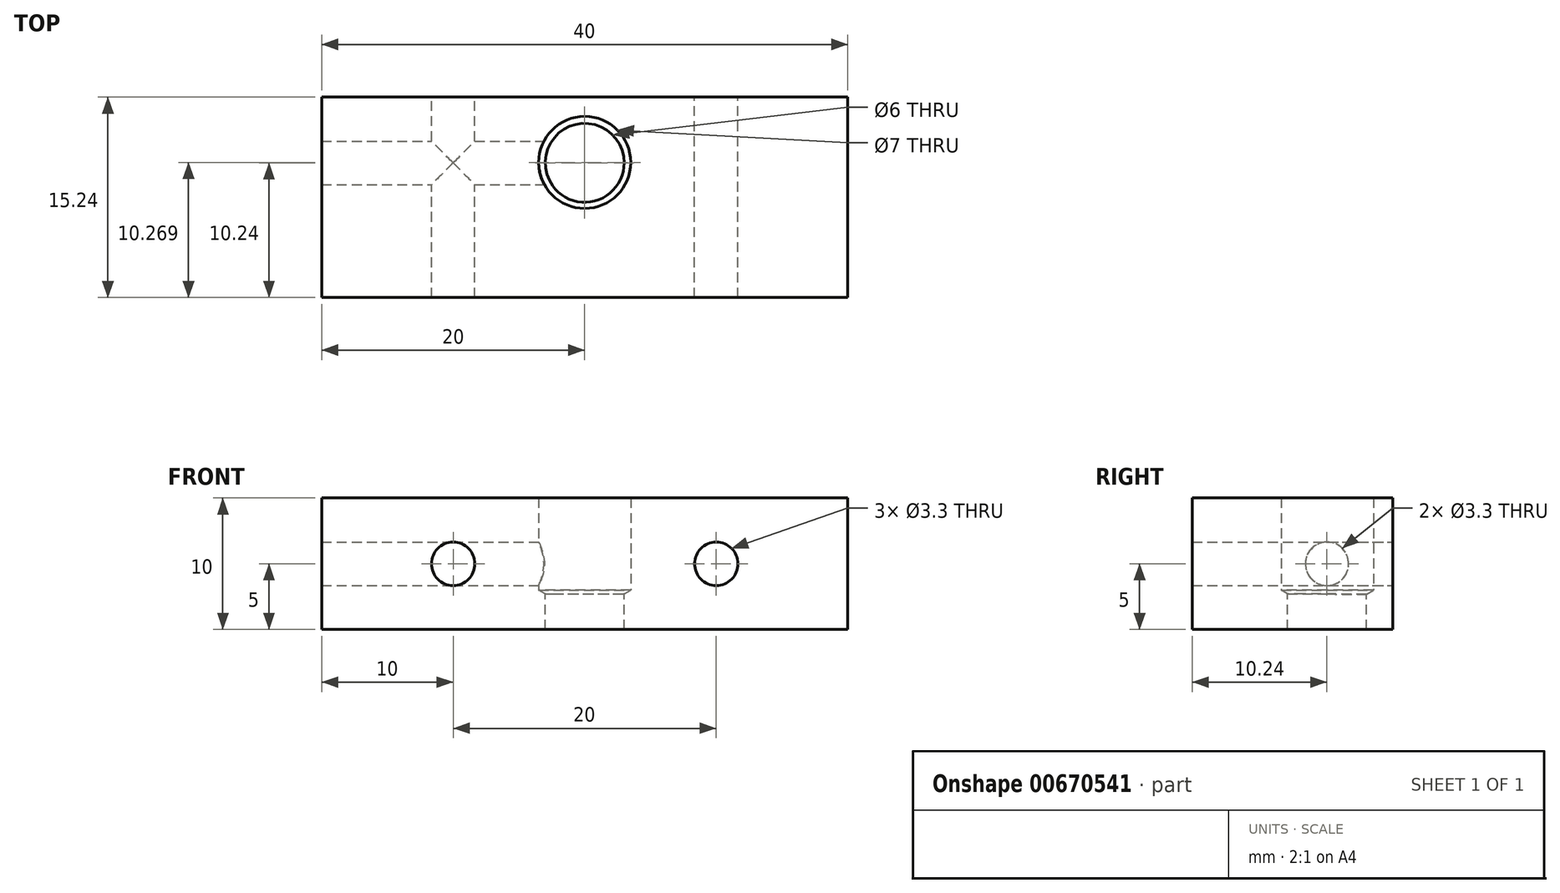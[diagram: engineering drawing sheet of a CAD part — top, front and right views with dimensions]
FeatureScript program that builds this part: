
annotation { "Feature Type Name" : "Feature", "Feature Type Description" : "" }
export const myFeature = defineFeature(function(context is Context, id is Id, definition is map)
    precondition{}
    {
        {
            var Q0;
            Q0=qCreatedBy(makeId("Top.planeOp"),FACE);
            var sketch = newSketch(context, id + "F0", { "sketchPlane" : qUnion([Q0])});
            skLineSegment(sketch, "E0.top", {"start": v(-20, -5) * mm, "end": v(20, -5) * mm});
            skLineSegment(sketch, "E0.left", {"start": v(-20, 10.24) * mm, "end": v(-20, -5) * mm});
            skLineSegment(sketch, "E0.right", {"start": v(20, 10.24) * mm, "end": v(20, -5) * mm});
            skLineSegment(sketch, "E1", {"start": v(-20, 10.24) * mm, "end": v(-9.42, 10.24) * mm});
            skLineSegment(sketch, "E2", {"start": v(20, 10.24) * mm, "end": v(10.65, 10.24) * mm});
            skLineSegment(sketch, "E3", {"start": v(-9.42, 10.24) * mm, "end": v(10.65, 10.24) * mm});
            skPoint(sketch, "E4", {"position": v(0, 5.24) * mm});
            skLineSegment(sketch, "E5.bottom", {"start": v(-20, 10.24) * mm, "end": v(-12, 10.24) * mm});
            skLineSegment(sketch, "E6.top", {"start": v(12, 10.24) * mm, "end": v(20, 10.24) * mm});
            skSolve(sketch);
        }
        {
            var Q0;
            Q0=makeQuery(id+"F0.imprint","IMPRINT",FACE,{"disambiguationData":[TD([[makeQuery(id+"F0.imprint","IMPRINT",EDGE,{"derivedFrom":sQuery(id+"F0.wireOp",EDGE,"E0.top")}),1.0]])]});
            extrude(context, id + "F1", {"entities" : qUnion([Q0]), "depth" : 10 * mm, "offsetDistance" : 25 * mm});
        }
        {
            var Q0;
            Q0=sQuery(id+"F0.wireOp",VERTEX,"E4");
            var Q1;
            Q1=makeQuery(id+"F1.opExtrude","SWEPT_BODY",BODY,{"disambiguationData":[OSD([sQuery(id+"F0.wireOp",EDGE,"E0.top"),sQuery(id+"F0.wireOp",EDGE,"E0.left"),sQuery(id+"F0.wireOp",EDGE,"E0.right"),sQuery(id+"F0.wireOp",EDGE,"E1"),sQuery(id+"F0.wireOp",EDGE,"E2"),sQuery(id+"F0.wireOp",EDGE,"E3")])]});
            hole(context, id + "F2", {"style" : HoleStyle.SIMPLE, "endStyle" : HoleEndStyle.THROUGH, "oppositeDirection" : true, "holeDiameter" : 6 * mm, "majorDiameter" : 5 * mm, "isTappedThrough" : true, "tappedDepth" : 10 * mm, "tapClearance" : 0, "locations" : qUnion([Q0]), "scope" : qUnion([Q1]), "startStyle" : HoleStartStyle.PART});
        }
        {
            var Q0;
            Q0=makeQuery(id+"F1.opExtrude","SWEPT_FACE",FACE,{"disambiguationData":[OSD([sQuery(id+"F0.wireOp",EDGE,"E0.top")])]});
            var sketch = newSketch(context, id + "F3", { "sketchPlane" : qUnion([Q0])});
            skPoint(sketch, "E7", {"position": v(-10, 5) * mm});
            skPoint(sketch, "E8", {"position": v(10, 5) * mm});
            skSolve(sketch);
        }
        {
            var Q0;
            Q0=sQuery(id+"F3.wireOp",VERTEX,"E7");
            var Q1;
            Q1=sQuery(id+"F3.wireOp",VERTEX,"E8");
            var Q2;
            Q2=makeQuery(id+"F1.opExtrude","SWEPT_BODY",BODY,{"disambiguationData":[OSD([sQuery(id+"F0.wireOp",EDGE,"E0.top"),sQuery(id+"F0.wireOp",EDGE,"E0.left"),sQuery(id+"F0.wireOp",EDGE,"E0.right"),sQuery(id+"F0.wireOp",EDGE,"E1"),sQuery(id+"F0.wireOp",EDGE,"E2"),sQuery(id+"F0.wireOp",EDGE,"E3"),sQuery(id+"F0.wireOp",EDGE,"E5.bottom"),sQuery(id+"F0.wireOp",EDGE,"E6.top")])]});
            hole(context, id + "F4", {"style" : HoleStyle.SIMPLE, "endStyle" : HoleEndStyle.BLIND, "standardTappedOrClearance" : lookupTablePath({ "standard" : "ISO", "engagement" : "75%", "pitch" : "0.7 mm", "size" : "M4", "type" : "Tapped" }), "standardBlindInLast" : lookupTablePath({ "standard" : "ISO", "engagement" : "75%", "pitch" : "0.7 mm", "size" : "M4", "type" : "Tapped" }), "holeDiameter" : 3.3 * mm, "majorDiameter" : 4 * mm, "showTappedDepth" : true, "holeDepth" : 15.5 * mm, "tappedDepth" : 15.5 * mm, "tapClearance" : 0, "locations" : qUnion([Q0, Q1]), "scope" : qUnion([Q2]), "startStyle" : HoleStartStyle.PART});
        }
        {
            var Q0;
            Q0=makeQuery(id+"F1.opExtrude","SWEPT_FACE",FACE,{"disambiguationData":[OSD([sQuery(id+"F0.wireOp",EDGE,"E0.left")])]});
            var sketch = newSketch(context, id + "F5", { "sketchPlane" : qUnion([Q0])});
            skPoint(sketch, "E9", {"position": v(-5.24, 5) * mm});
            skPoint(sketch, "E9.positionSnap0", {"position": v(-10.24, 5) * mm});
            skSolve(sketch);
        }
        {
            var Q0;
            Q0=sQuery(id+"F5.wireOp",VERTEX,"E9");
            var Q1;
            Q1=makeQuery(id+"F1.opExtrude","SWEPT_BODY",BODY,{"disambiguationData":[OSD([sQuery(id+"F0.wireOp",EDGE,"E0.top"),sQuery(id+"F0.wireOp",EDGE,"E0.left"),sQuery(id+"F0.wireOp",EDGE,"E0.right"),sQuery(id+"F0.wireOp",EDGE,"E1"),sQuery(id+"F0.wireOp",EDGE,"E2"),sQuery(id+"F0.wireOp",EDGE,"E3"),sQuery(id+"F0.wireOp",EDGE,"E5.bottom"),sQuery(id+"F0.wireOp",EDGE,"E6.top")])]});
            hole(context, id + "F6", {"style" : HoleStyle.SIMPLE, "endStyle" : HoleEndStyle.BLIND, "standardTappedOrClearance" : lookupTablePath({ "standard" : "ISO", "engagement" : "75%", "pitch" : "0.7 mm", "size" : "M4", "type" : "Tapped" }), "standardBlindInLast" : lookupTablePath({ "standard" : "ISO", "engagement" : "75%", "pitch" : "0.7 mm", "size" : "M4", "type" : "Tapped" }), "holeDiameter" : 3.3 * mm, "majorDiameter" : 4 * mm, "showTappedDepth" : true, "holeDepth" : 20 * mm, "tappedDepth" : 20 * mm, "tapClearance" : 0, "locations" : qUnion([Q0]), "scope" : qUnion([Q1]), "startStyle" : HoleStartStyle.PART});
        }
        {
            var Q0;
            Q0=makeQuery(id+"F1.opExtrude","CAP_FACE",FACE,{"disambiguationData":[OSD([sQuery(id+"F0.wireOp",EDGE,"E0.top"),sQuery(id+"F0.wireOp",EDGE,"E0.left"),sQuery(id+"F0.wireOp",EDGE,"E0.right"),sQuery(id+"F0.wireOp",EDGE,"E1"),sQuery(id+"F0.wireOp",EDGE,"E2"),sQuery(id+"F0.wireOp",EDGE,"E3"),sQuery(id+"F0.wireOp",EDGE,"E5.bottom"),sQuery(id+"F0.wireOp",EDGE,"E6.top")])],"isStart":false});
            var sketch = newSketch(context, id + "F7", { "sketchPlane" : qUnion([Q0])});
            skSolve(sketch);
        }
        {
            var Q0;
            {var subQ7=sQuery(id+"F0.wireOp",EDGE,"E0.top");Q0=makeQuery(id+"F7.imprint","IMPRINT",FACE,{"disambiguationData":[TD([[makeQuery(id+"F7.imprint","IMPRINT",EDGE,{"derivedFrom":makeQuery(id+"F1.opExtrude","CAP_EDGE",EDGE,{"disambiguationData":[OSD([subQ7])],"isStart":false})}),1.0]])]});}
            var sketch = newSketch(context, id + "F8", { "sketchPlane" : qUnion([Q0])});
            skPoint(sketch, "E10", {"position": v(0, 5.27) * mm});
            skSolve(sketch);
        }
        {
            var Q0;
            Q0=sQuery(id+"F8.wireOp",VERTEX,"E10");
            var Q1;
            Q1=makeQuery(id+"F1.opExtrude","SWEPT_BODY",BODY,{"disambiguationData":[OSD([sQuery(id+"F0.wireOp",EDGE,"E0.top"),sQuery(id+"F0.wireOp",EDGE,"E0.left"),sQuery(id+"F0.wireOp",EDGE,"E0.right"),sQuery(id+"F0.wireOp",EDGE,"E1"),sQuery(id+"F0.wireOp",EDGE,"E2"),sQuery(id+"F0.wireOp",EDGE,"E3"),sQuery(id+"F0.wireOp",EDGE,"E5.bottom"),sQuery(id+"F0.wireOp",EDGE,"E6.top")])]});
            hole(context, id + "F9", {"style" : HoleStyle.SIMPLE, "endStyle" : HoleEndStyle.BLIND, "holeDiameter" : 7 * mm, "majorDiameter" : 5 * mm, "holeDepth" : 7 * mm, "isTappedThrough" : true, "tappedDepth" : 15 * mm, "tapClearance" : 3, "locations" : qUnion([Q0]), "scope" : qUnion([Q1]), "startStyle" : HoleStartStyle.PART});
        }
    });
